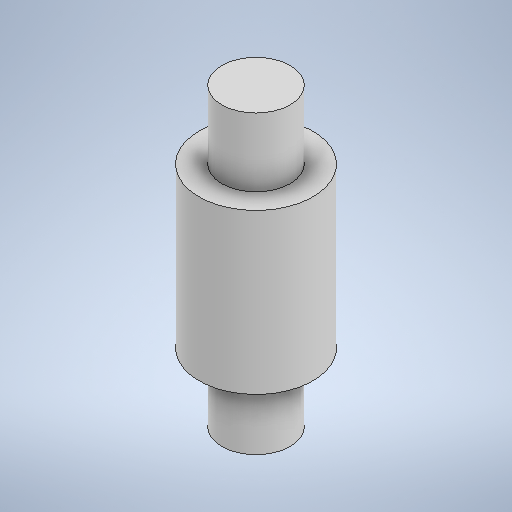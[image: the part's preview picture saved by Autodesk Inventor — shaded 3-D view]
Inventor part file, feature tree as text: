
AUTODESK INVENTOR PART (.ipt)
format: ipt  version: 2025 (Build 290162010, 162A)  size: 250,368 bytes
history: native  units: mm
features: revolve x1, sketch x1
ambient origin geometry x8: Origin, YZ Plane, XZ Plane, XY Plane, X Axis, Y Axis, Z Axis, Center Point
bodies: Solid1 (feature_tree)
feature tree (2):
  revolve  "Revolution1"  [1 undecoded]
  sketch  "Sketch1"  dims[d1=3.0mm d2=7.0mm d3=3.0mm d4=3.0mm d5=5.0mm d6=90.0deg]
note: 1 required parameter value undecoded (feature->parameter linkage not recoverable at this tier; creation-order binding heuristic only, values carry confidence <= 0.55)
